# Revit family: Bench_Triangle_Noble
name_source: partatom
category: Specialty Equipment
revit_build: Autodesk Revit 2016 (Build: 20150714_1515(x64)
units: mm (PartAtom-declared; Revit-internal decimal feet)

## family parameters
Cut with Voids When Loaded = No
Host = Face
OmniClass Number = 23.45.55.21
OmniClass Title = Drains (Wastes)
Part Type = Normal
Room Calculation Point = No
Round Connector Dimension = Use Diameter
Shared = No

## types (2) — shared parameters
Assembly Code = D2030300
Base = Polymer coated Expanded Polystyrene
Building Codes = http://www.noblecompany.com
Default Elevation = 0"
Description = Freestyle 24 ABS - Wave Linear Drain
Height = 20"
Installation-Fabrication = http://www.noblecompany.com
Manufacturer = Noble Company
Manufacturer Fax = 231-799-8850
Product Data = http://www.noblecompany.com
Product Properties = http://www.noblecompany.com
Triangle = Yes
URL = www.noblecompany.com

## per-type parameters (varying)
| type | Length | Width |
| Large Triangular #402 | 32 1/2" | 32 1/2" |
| Small Triangular #400 | 22" | 22" |

## geometry (parser evidence)
native form markers: Sweep x6
no freeform markers — native parametric forms only
